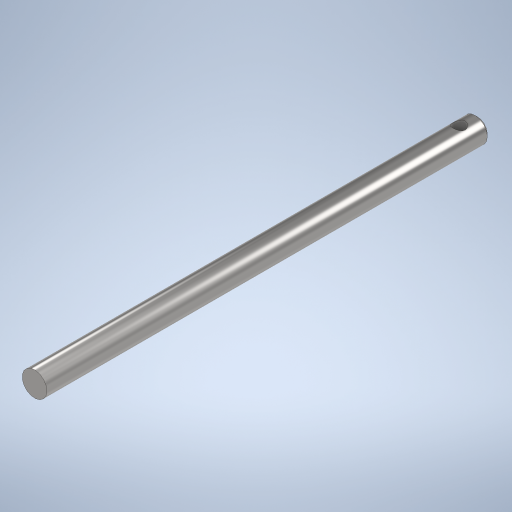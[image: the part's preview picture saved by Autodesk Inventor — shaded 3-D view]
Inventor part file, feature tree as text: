
AUTODESK INVENTOR PART (.ipt)
format: ipt  version: 2023 (Build 270158030, 158C)  size: 286,720 bytes
history: mixed  units: in
note: dims shown in document units (in); Inventor stores cm internally (conversion verified against a paired STEP export)
features: extrude x2, sketch x2, chamfer x1, imported_body x1
ambient origin geometry x8: Origin, YZ Plane, XZ Plane, XY Plane, X Axis, Y Axis, Z Axis, Center Point
bodies: Solid1 (imported_parasolid)
feature tree (6):
  extrude  "Extrusion2"  Depth=0.1969in
  extrude  "Extrusion3"  Depth=0.7874in TaperAngle=0.0deg
  sketch  "Sketch3"  dims[d3=0.1969in d4=0.2953in]
  sketch  "Sketch5"  dims[d5=0.0in d6=0.0in d10=0.7874in d11=0.0in]
  chamfer  "Chamfer1"  [1 undecoded]
  imported_body  NMx_Import_Brep_tag  [imported B-rep: ~5 faces, bbox_mm=None]
note: 1 required parameter value undecoded (feature->parameter linkage not recoverable at this tier; creation-order binding heuristic only, values carry confidence <= 0.55)
